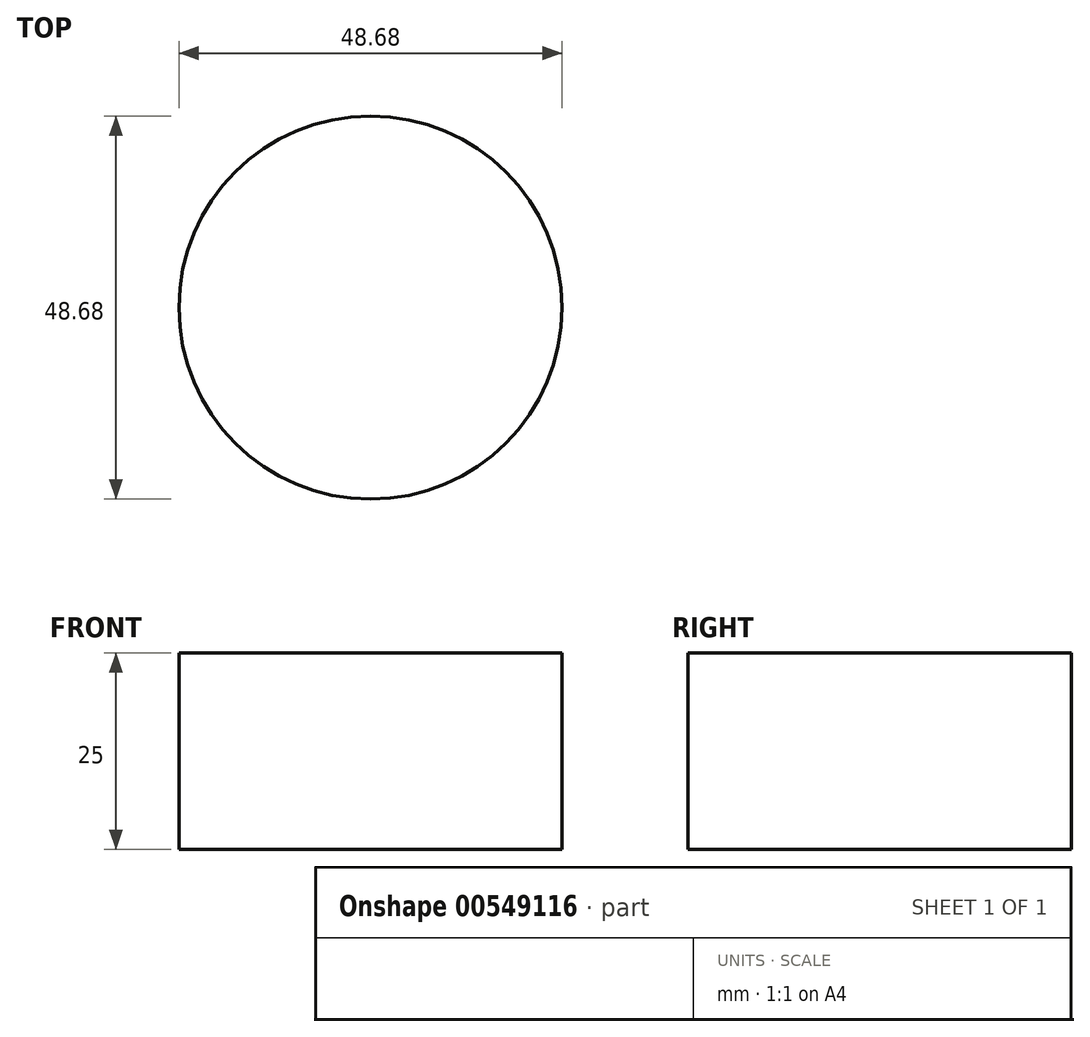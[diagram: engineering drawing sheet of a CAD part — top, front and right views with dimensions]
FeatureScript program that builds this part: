
annotation { "Feature Type Name" : "Feature", "Feature Type Description" : "" }
export const myFeature = defineFeature(function(context is Context, id is Id, definition is map)
    precondition{}
    {
        {
            var Q0;
            Q0=qCreatedBy(makeId("Top.planeOp"),FACE);
            var sketch = newSketch(context, id + "F0", { "sketchPlane" : qUnion([Q0])});
            skCircle(sketch, "E0", {"center": v(-38.06, 23.39) * mm, "radius": 24.34 * mm});
            skSolve(sketch);
        }
        {
            var Q0;
            Q0=makeQuery(id+"F0.imprint","IMPRINT",FACE,{"disambiguationData":[TD([[makeQuery(id+"F0.imprint","IMPRINT",EDGE,{"derivedFrom":sQuery(id+"F0.wireOp",EDGE,"E0")}),1.0]])]});
            extrude(context, id + "F1", {"entities" : qUnion([Q0]), "depth" : 25 * mm, "offsetDistance" : 25 * mm});
        }
    });
